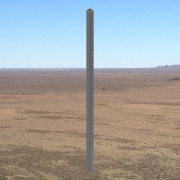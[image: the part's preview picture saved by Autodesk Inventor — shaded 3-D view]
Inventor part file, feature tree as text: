
AUTODESK INVENTOR PART (.ipt)
format: ipt  version: 2014 SP1 (Build 180222100, 222)  size: 269,312 bytes
history: native  units: in
note: dims shown in document units (in); Inventor stores cm internally (conversion verified against a paired STEP export)
features: sketch x3, hole x2, pattern_linear x2, extrude x1
ambient origin geometry x8: Origin, YZ Plane, XZ Plane, XY Plane, X Axis, Y Axis, Z Axis, Center Point
bodies: Solid1 (feature_tree)
feature tree (8):
  extrude  "Extrusion1"  Depth=1.0in
  hole  "Hole1"  [1 undecoded]
  pattern_linear  "Rectangular Pattern1"  Spacing1=1.0in  [1 undecoded]
  hole  "Hole2"  [1 undecoded]
  pattern_linear  "Rectangular Pattern2"  Spacing1=1.0in  [1 undecoded]
  sketch  "Sketch1"  dims[d0=1.0in d1=1.0in]
  sketch  "Sketch2"  dims[d2=0.125in d3=36.0in d4=0.0in]
  sketch  "Sketch3"  dims[d5=0.25in d6=1.0in d7=0.25in d8=0.75in d9=0.375in d10=0.25in d11=0.5635in d12=1.0in d13=0.8108in d14=13.7795in d16=1.0in d17=1.0in d18=0.25in d19=0.75in d20=0.375in d21=0.25in d22=0.5635in d23=1.0in d24=0.8108in d25=13.7795in d27=1.0in]
note: 4 required parameter values undecoded (feature->parameter linkage not recoverable at this tier; creation-order binding heuristic only, values carry confidence <= 0.55)
